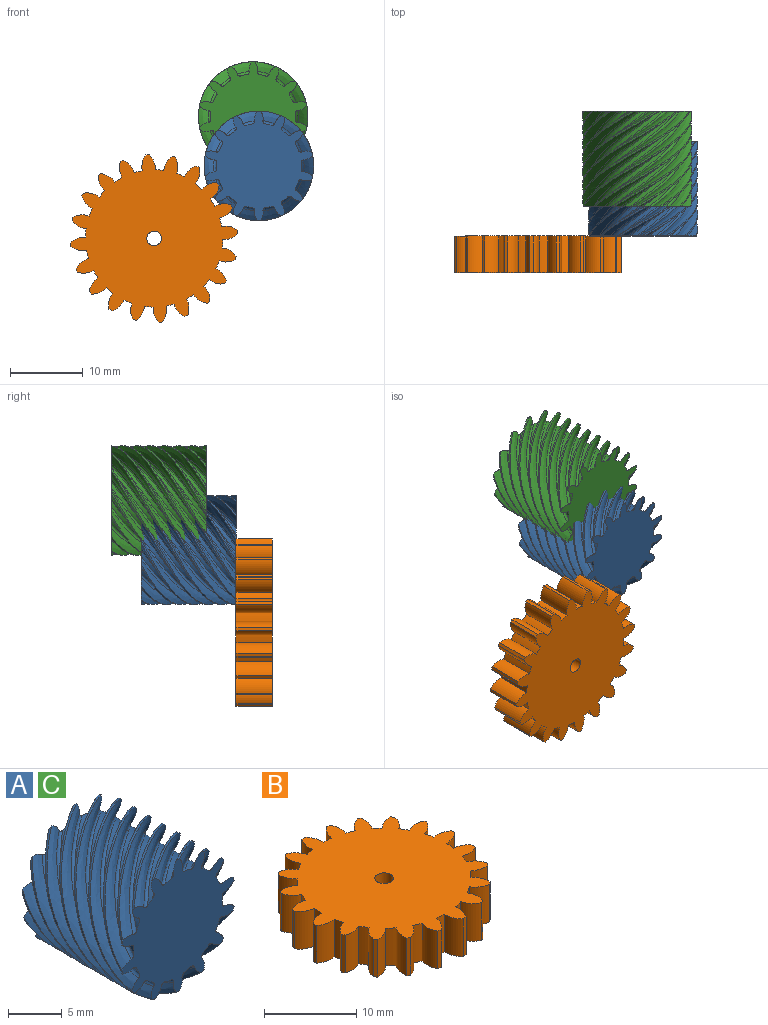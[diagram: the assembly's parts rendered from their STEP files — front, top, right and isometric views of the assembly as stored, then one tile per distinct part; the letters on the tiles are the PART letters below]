
ASSEMBLY  parts=3 mates=1
PART A: 114 faces, bbox 15.8x13.5x15.8 mm
  f0: cylinder r=5.81mm len=13mm, axis (0,1,0), area 11.1mm2, adj f14,f15,f19,f113
  f1: cylinder r=5.81mm len=13mm, axis (0,1,0), area 11.1mm2, adj f14,f15,f106,f110
  f2: cylinder r=5.81mm len=13mm, axis (0,1,0), area 11.1mm2, adj f14,f15,f99,f103
  f3: cylinder r=5.81mm len=13mm, axis (0,1,0), area 11.1mm2, adj f14,f15,f92,f96
  f4: cylinder r=5.81mm len=13mm, axis (0,1,0), area 11.1mm2, adj f14,f15,f85,f89
  f5: cylinder r=5.81mm len=13mm, axis (0,1,0), area 11.1mm2, adj f14,f15,f78,f82
  f6: cylinder r=5.81mm len=13mm, axis (0,1,0), area 11.1mm2, adj f14,f15,f71,f75
  f7: cylinder r=5.81mm len=13mm, axis (0,1,0), area 11.1mm2, adj f14,f15,f64,f68
  f8: cylinder r=5.81mm len=13mm, axis (0,1,0), area 11.1mm2, adj f14,f15,f57,f61
  f9: cylinder r=5.81mm len=13mm, axis (0,1,0), area 11.1mm2, adj f14,f15,f50,f54
  f10: cylinder r=5.81mm len=13mm, axis (0,1,0), area 11.1mm2, adj f14,f15,f43,f47
  f11: cylinder r=5.81mm len=13mm, axis (0,1,0), area 11.1mm2, adj f14,f15,f36,f40
  f12: cylinder r=5.81mm len=13mm, axis (0,1,0), area 11.1mm2, adj f14,f15,f29,f33
  f13: cylinder r=5.81mm len=13mm, axis (0,1,0), area 11.1mm2, adj f14,f15,f22,f26
  f14: plane 15.02x14.73mm, normal (0,-1,0), area 130.6mm2, adj f0,f1,f2,f3,f4,f5,f6,f7
  f15: plane 15.01x14.92mm, normal (0,1,0), area 129.4mm2, adj f0,f1,f2,f3,f4,f5,f6,f7
  f16: cylinder r=7.5mm len=14.99mm, axis (0,1,0), area 5.5mm2, adj f14,f15,f17,f18
  f17: bspline ~15.06x13.32mm, area 33mm2, adj f14,f15,f16,f22
  f18: bspline ~15.08x13.32mm, area 33mm2, adj f14,f15,f16,f19
  f19: bspline ~13.46x12.53mm, area 10.7mm2, adj f0,f14,f15,f18,f20
  f20: plane 0.44x0.4mm, normal (0,1,0), area 0mm2, adj f15,f19
  f21: plane 0.45x0.42mm, normal (0,1,0), area 0mm2, adj f15,f22
  f22: bspline ~13x12.36mm, area 10.7mm2, adj f13,f14,f17,f21
  f23: cylinder r=7.5mm len=14.35mm, axis (0,1,0), area 5.5mm2, adj f14,f15,f24,f25
  f24: bspline ~14.45x13.32mm, area 33mm2, adj f14,f15,f23,f29
  f25: bspline ~14.35x13.01mm, area 33mm2, adj f14,f15,f23,f26
  f26: bspline ~13.32x12.31mm, area 10.7mm2, adj f13,f14,f15,f25,f27
  f27: plane 0.45x0.34mm, normal (0,1,0), area 0mm2, adj f15,f26
  f28: plane 0.53x0.39mm, normal (0,1,0), area 0mm2, adj f15,f29
  f29: bspline ~13x11.51mm, area 10.7mm2, adj f12,f14,f24,f28
  f30: cylinder r=7.5mm len=13.13mm, axis (0,1,0), area 5.5mm2, adj f14,f15,f31,f32
  f31: bspline ~13.53x13.32mm, area 33mm2, adj f14,f15,f30,f36
  f32: bspline ~13.01x12.85mm, area 33mm2, adj f14,f15,f30,f33
  f33: bspline ~13.01x10.48mm, area 10.7mm2, adj f12,f14,f15,f32,f34
  f34: plane 0.5x0.31mm, normal (0,1,0), area 0mm2, adj f15,f33
  f35: plane 0.54x0.37mm, normal (0,1,0), area 0mm2, adj f15,f36
  f36: bspline ~13x11.09mm, area 10.7mm2, adj f11,f14,f31,f35
  f37: cylinder r=7.5mm len=14.72mm, axis (0,1,0), area 5.5mm2, adj f14,f15,f38,f39
  f38: bspline ~15.19x13.32mm, area 33mm2, adj f14,f15,f37,f43
  f39: bspline ~15.16x13.32mm, area 33mm2, adj f14,f15,f37,f40
  f40: bspline ~13.46x12.42mm, area 10.7mm2, adj f11,f14,f15,f39,f41
  f41: plane 0.46x0.41mm, normal (0,1,0), area 0mm2, adj f15,f40
  f42: plane 0.44x0.41mm, normal (0,1,0), area 0mm2, adj f15,f43
  f43: bspline ~13x12.26mm, area 10.8mm2, adj f10,f14,f38,f42
  f44: cylinder r=7.5mm len=14.86mm, axis (0,1,0), area 5.5mm2, adj f14,f15,f45,f46
  f45: bspline ~15.13x13.32mm, area 33mm2, adj f14,f15,f44,f50
  f46: bspline ~14.85x13.01mm, area 33mm2, adj f14,f15,f44,f47
  f47: bspline ~13.01x12.33mm, area 10.7mm2, adj f10,f14,f15,f46,f48
  f48: plane 0.45x0.34mm, normal (0,1,0), area 0mm2, adj f15,f47
  f49: plane 0.49x0.43mm, normal (0,1,0), area 0mm2, adj f15,f50
  f50: bspline ~13x12.08mm, area 10.7mm2, adj f9,f14,f45,f49
  f51: cylinder r=7.5mm len=13.49mm, axis (0,1,0), area 5.5mm2, adj f14,f15,f52,f53
  f52: bspline ~13.39x13.32mm, area 33mm2, adj f14,f15,f51,f57
  f53: bspline ~13.49x13.01mm, area 33mm2, adj f14,f15,f51,f54
  f54: bspline ~13.01x11.37mm, area 10.7mm2, adj f9,f14,f15,f53,f55
  f55: plane 0.49x0.33mm, normal (0,1,0), area 0mm2, adj f15,f54
  f56: plane 0.55x0.34mm, normal (0,1,0), area 0mm2, adj f15,f57
  f57: bspline ~13x10.67mm, area 10.7mm2, adj f8,f14,f52,f56
  f58: cylinder r=7.5mm len=14.09mm, axis (0,1,0), area 5.5mm2, adj f14,f15,f59,f60
  f59: bspline ~14.69x13.32mm, area 33mm2, adj f14,f15,f58,f64
  f60: bspline ~14.47x13.32mm, area 33mm2, adj f14,f15,f58,f61
  f61: bspline ~13.46x11.68mm, area 10.7mm2, adj f8,f14,f15,f60,f62
  f62: plane 0.49x0.36mm, normal (0,1,0), area 0mm2, adj f15,f61
  f63: plane 0.5x0.4mm, normal (0,1,0), area 0mm2, adj f15,f64
  f64: bspline ~13x11.82mm, area 10.7mm2, adj f7,f14,f59,f63
  f65: cylinder r=7.5mm len=14.99mm, axis (0,1,0), area 5.5mm2, adj f14,f15,f66,f67
  f66: bspline ~15.06x13.32mm, area 33mm2, adj f14,f15,f65,f71
  f67: bspline ~15.08x13.32mm, area 33mm2, adj f14,f15,f65,f68
  f68: bspline ~13.46x12.53mm, area 10.7mm2, adj f7,f14,f15,f67,f69
  f69: plane 0.44x0.4mm, normal (0,1,0), area 0mm2, adj f15,f68
  f70: plane 0.44x0.42mm, normal (0,1,0), area 0mm2, adj f15,f71
  f71: bspline ~13x12.36mm, area 10.7mm2, adj f6,f14,f66,f70
  f72: cylinder r=7.5mm len=14.35mm, axis (0,1,0), area 5.5mm2, adj f14,f15,f73,f74
  f73: bspline ~14.45x13.32mm, area 33mm2, adj f14,f15,f72,f78
  f74: bspline ~14.35x13.01mm, area 33mm2, adj f14,f15,f72,f75
  f75: bspline ~13.32x12.31mm, area 10.7mm2, adj f6,f14,f15,f74,f76
  f76: plane 0.45x0.34mm, normal (0,1,0), area 0mm2, adj f15,f75
  f77: plane 0.53x0.39mm, normal (0,1,0), area 0mm2, adj f15,f78
  f78: bspline ~13x11.51mm, area 10.7mm2, adj f5,f14,f73,f77
  f79: cylinder r=7.5mm len=13.13mm, axis (0,1,0), area 5.5mm2, adj f14,f15,f80,f81
  f80: bspline ~13.53x13.32mm, area 33mm2, adj f14,f15,f79,f85
  f81: bspline ~13.01x12.85mm, area 33mm2, adj f14,f15,f79,f82
  f82: bspline ~13.01x10.48mm, area 10.7mm2, adj f5,f14,f15,f81,f83
  f83: plane 0.5x0.31mm, normal (0,1,0), area 0mm2, adj f15,f82
  f84: plane 0.54x0.37mm, normal (0,1,0), area 0mm2, adj f15,f85
  f85: bspline ~13x11.09mm, area 10.7mm2, adj f4,f14,f80,f84
  f86: cylinder r=7.5mm len=14.72mm, axis (0,1,0), area 5.5mm2, adj f14,f15,f87,f88
  f87: bspline ~15.19x13.32mm, area 33mm2, adj f14,f15,f86,f92
  f88: bspline ~15.16x13.32mm, area 33mm2, adj f14,f15,f86,f89
  f89: bspline ~13.46x12.42mm, area 10.7mm2, adj f4,f14,f15,f88,f90
  f90: plane 0.46x0.41mm, normal (0,1,0), area 0mm2, adj f15,f89
  f91: plane 0.44x0.41mm, normal (0,1,0), area 0mm2, adj f15,f92
  f92: bspline ~13x12.26mm, area 10.8mm2, adj f3,f14,f87,f91
  f93: cylinder r=7.5mm len=14.86mm, axis (0,1,0), area 5.5mm2, adj f14,f15,f94,f95
  f94: bspline ~15.13x13.32mm, area 33mm2, adj f14,f15,f93,f99
  f95: bspline ~14.85x13.01mm, area 33mm2, adj f14,f15,f93,f96
  f96: bspline ~13.01x12.33mm, area 10.7mm2, adj f3,f14,f15,f95,f97
  f97: plane 0.45x0.34mm, normal (0,1,0), area 0mm2, adj f15,f96
  f98: plane 0.49x0.43mm, normal (0,1,0), area 0mm2, adj f15,f99
  f99: bspline ~13x12.08mm, area 10.7mm2, adj f2,f14,f94,f98
  f100: cylinder r=7.5mm len=13.49mm, axis (0,1,0), area 5.5mm2, adj f14,f15,f101,f102
  f101: bspline ~13.39x13.32mm, area 33mm2, adj f14,f15,f100,f106
  f102: bspline ~13.49x13.01mm, area 33mm2, adj f14,f15,f100,f103
  f103: bspline ~13.01x11.37mm, area 10.7mm2, adj f2,f14,f15,f102,f104
  f104: plane 0.49x0.33mm, normal (0,1,0), area 0mm2, adj f15,f103
  f105: plane 0.55x0.34mm, normal (0,1,0), area 0mm2, adj f15,f106
  f106: bspline ~13x10.67mm, area 10.7mm2, adj f1,f14,f101,f105
  f107: cylinder r=7.5mm len=14.09mm, axis (0,1,0), area 5.5mm2, adj f14,f15,f108,f109
  f108: bspline ~14.69x13.32mm, area 33mm2, adj f14,f15,f107,f113
  f109: bspline ~14.47x13.32mm, area 33mm2, adj f14,f15,f107,f110
  f110: bspline ~13.46x11.68mm, area 10.7mm2, adj f1,f14,f15,f109,f111
  f111: plane 0.49x0.36mm, normal (0,1,0), area 0mm2, adj f15,f110
  f112: plane 0.5x0.4mm, normal (0,1,0), area 0mm2, adj f15,f113
  f113: bspline ~13x11.82mm, area 10.7mm2, adj f0,f14,f108,f112
PART B: 83 faces, bbox 23x23x5 mm
  f0: cylinder r=2.61mm len=5mm, axis (0,0,-1), area 11.5mm2, adj f1,f79,f81,f82
  f1: cylinder r=9.41mm len=5mm, axis (0,0,-1), area 5.9mm2, adj f0,f2,f81,f82
  f2: cylinder r=2.61mm len=5mm, axis (0,0,-1), area 11.5mm2, adj f1,f3,f81,f82
  f3: plane 5x0.41mm, normal (-0.38,0.92,0), area 2.2mm2, adj f2,f4,f81,f82
  f4: cylinder r=2.61mm len=5mm, axis (0,0,-1), area 11.5mm2, adj f3,f5,f81,f82
  f5: cylinder r=9.41mm len=5mm, axis (0,0,-1), area 5.9mm2, adj f4,f6,f81,f82
  f6: cylinder r=2.61mm len=5mm, axis (0,0,-1), area 11.5mm2, adj f5,f7,f81,f82
  f7: plane 5x0.34mm, normal (-0.65,0.76,0), area 2.2mm2, adj f6,f8,f81,f82
  f8: cylinder r=2.61mm len=5mm, axis (0,0,-1), area 11.5mm2, adj f7,f9,f81,f82
  f9: cylinder r=9.41mm len=5mm, axis (0,0,-1), area 5.9mm2, adj f8,f10,f81,f82
  f10: cylinder r=2.61mm len=5mm, axis (0,0,-1), area 11.5mm2, adj f9,f11,f81,f82
  f11: plane 5x0.38mm, normal (-0.85,0.52,0), area 2.2mm2, adj f10,f12,f81,f82
  f12: cylinder r=2.61mm len=5mm, axis (0,0,-1), area 11.5mm2, adj f11,f13,f81,f82
  f13: cylinder r=9.41mm len=5mm, axis (0,0,-1), area 5.9mm2, adj f12,f14,f81,f82
  f14: cylinder r=2.61mm len=5mm, axis (0,0,-1), area 11.5mm2, adj f13,f15,f81,f82
  f15: plane 5x0.43mm, normal (-0.97,0.23,0), area 2.2mm2, adj f14,f16,f81,f82
  f16: cylinder r=2.61mm len=5mm, axis (0,0,-1), area 11.5mm2, adj f15,f17,f81,f82
  f17: cylinder r=9.41mm len=5mm, axis (0,0,-1), area 5.9mm2, adj f16,f18,f81,f82
  f18: cylinder r=2.61mm len=5mm, axis (0,0,-1), area 11.5mm2, adj f17,f19,f81,f82
  f19: plane 5x0.44mm, normal (-1,-0.08,0), area 2.2mm2, adj f18,f20,f81,f82
  f20: cylinder r=2.61mm len=5mm, axis (0,0,-1), area 11.5mm2, adj f19,f21,f81,f82
  f21: cylinder r=9.41mm len=5mm, axis (0,0,-1), area 5.9mm2, adj f20,f22,f81,f82
  f22: cylinder r=2.61mm len=5mm, axis (0,0,-1), area 11.5mm2, adj f21,f23,f81,f82
  f23: plane 5x0.41mm, normal (-0.92,-0.38,0), area 2.2mm2, adj f22,f24,f81,f82
  f24: cylinder r=2.61mm len=5mm, axis (0,0,-1), area 11.5mm2, adj f23,f25,f81,f82
  f25: cylinder r=9.41mm len=5mm, axis (0,0,-1), area 5.9mm2, adj f24,f26,f81,f82
  f26: cylinder r=2.61mm len=5mm, axis (0,0,-1), area 11.5mm2, adj f25,f27,f81,f82
  f27: plane 5x0.34mm, normal (-0.76,-0.65,0), area 2.2mm2, adj f26,f28,f81,f82
  f28: cylinder r=2.61mm len=5mm, axis (0,0,-1), area 11.5mm2, adj f27,f29,f81,f82
  f29: cylinder r=9.41mm len=5mm, axis (0,0,-1), area 5.9mm2, adj f28,f30,f81,f82
  f30: cylinder r=2.61mm len=5mm, axis (0,0,-1), area 11.5mm2, adj f29,f31,f81,f82
  f31: plane 5x0.38mm, normal (-0.52,-0.85,0), area 2.2mm2, adj f30,f32,f81,f82
  f32: cylinder r=2.61mm len=5mm, axis (0,0,-1), area 11.5mm2, adj f31,f33,f81,f82
  f33: cylinder r=9.41mm len=5mm, axis (0,0,-1), area 5.9mm2, adj f32,f34,f81,f82
  f34: cylinder r=2.61mm len=5mm, axis (0,0,-1), area 11.5mm2, adj f33,f35,f81,f82
  f35: plane 5x0.43mm, normal (-0.23,-0.97,0), area 2.2mm2, adj f34,f36,f81,f82
  f36: cylinder r=2.61mm len=5mm, axis (0,0,-1), area 11.5mm2, adj f35,f37,f81,f82
  f37: cylinder r=9.41mm len=5mm, axis (0,0,-1), area 5.9mm2, adj f36,f38,f81,f82
  f38: cylinder r=2.61mm len=5mm, axis (0,0,-1), area 11.5mm2, adj f37,f39,f81,f82
  f39: plane 5x0.44mm, normal (0.08,-1,0), area 2.2mm2, adj f38,f40,f81,f82
  f40: cylinder r=2.61mm len=5mm, axis (0,0,-1), area 11.5mm2, adj f39,f41,f81,f82
  f41: cylinder r=9.41mm len=5mm, axis (0,0,-1), area 5.9mm2, adj f40,f42,f81,f82
  f42: cylinder r=2.61mm len=5mm, axis (0,0,-1), area 11.5mm2, adj f41,f43,f81,f82
  f43: plane 5x0.41mm, normal (0.38,-0.92,0), area 2.2mm2, adj f42,f44,f81,f82
  f44: cylinder r=2.61mm len=5mm, axis (0,0,-1), area 11.5mm2, adj f43,f45,f81,f82
  f45: cylinder r=9.41mm len=5mm, axis (0,0,-1), area 5.9mm2, adj f44,f46,f81,f82
  f46: cylinder r=2.61mm len=5mm, axis (0,0,-1), area 11.5mm2, adj f45,f47,f81,f82
  f47: plane 5x0.34mm, normal (0.65,-0.76,0), area 2.2mm2, adj f46,f48,f81,f82
  f48: cylinder r=2.61mm len=5mm, axis (0,0,-1), area 11.5mm2, adj f47,f49,f81,f82
  f49: cylinder r=9.41mm len=5mm, axis (0,0,-1), area 5.9mm2, adj f48,f50,f81,f82
  f50: cylinder r=2.61mm len=5mm, axis (0,0,-1), area 11.5mm2, adj f49,f51,f81,f82
  f51: plane 5x0.38mm, normal (0.85,-0.52,0), area 2.2mm2, adj f50,f52,f81,f82
  f52: cylinder r=2.61mm len=5mm, axis (0,0,-1), area 11.5mm2, adj f51,f53,f81,f82
  f53: cylinder r=9.41mm len=5mm, axis (0,0,-1), area 5.9mm2, adj f52,f54,f81,f82
  f54: cylinder r=2.61mm len=5mm, axis (0,0,-1), area 11.5mm2, adj f53,f55,f81,f82
  f55: plane 5x0.43mm, normal (0.97,-0.23,0), area 2.2mm2, adj f54,f56,f81,f82
  f56: cylinder r=2.61mm len=5mm, axis (0,0,-1), area 11.5mm2, adj f55,f57,f81,f82
  f57: cylinder r=9.41mm len=5mm, axis (0,0,-1), area 5.9mm2, adj f56,f58,f81,f82
  f58: cylinder r=2.61mm len=5mm, axis (0,0,-1), area 11.5mm2, adj f57,f59,f81,f82
  f59: plane 5x0.44mm, normal (1,0.08,0), area 2.2mm2, adj f58,f60,f81,f82
  f60: cylinder r=2.61mm len=5mm, axis (0,0,-1), area 11.5mm2, adj f59,f61,f81,f82
  f61: cylinder r=9.41mm len=5mm, axis (0,0,-1), area 5.9mm2, adj f60,f62,f81,f82
  f62: cylinder r=2.61mm len=5mm, axis (0,0,-1), area 11.5mm2, adj f61,f63,f81,f82
  f63: plane 5x0.41mm, normal (0.92,0.38,0), area 2.2mm2, adj f62,f64,f81,f82
  f64: cylinder r=2.61mm len=5mm, axis (0,0,-1), area 11.5mm2, adj f63,f65,f81,f82
  f65: cylinder r=9.41mm len=5mm, axis (0,0,-1), area 5.9mm2, adj f64,f66,f81,f82
  f66: cylinder r=2.61mm len=5mm, axis (0,0,-1), area 11.5mm2, adj f65,f67,f81,f82
  f67: plane 5x0.34mm, normal (0.76,0.65,0), area 2.2mm2, adj f66,f68,f81,f82
  f68: cylinder r=2.61mm len=5mm, axis (0,0,-1), area 11.5mm2, adj f67,f69,f81,f82
  f69: cylinder r=9.41mm len=5mm, axis (0,0,-1), area 5.9mm2, adj f68,f70,f81,f82
  f70: cylinder r=2.61mm len=5mm, axis (0,0,-1), area 11.5mm2, adj f69,f71,f81,f82
  f71: plane 5x0.38mm, normal (0.52,0.85,0), area 2.2mm2, adj f70,f72,f81,f82
  f72: cylinder r=2.61mm len=5mm, axis (0,0,-1), area 11.5mm2, adj f71,f73,f81,f82
  f73: cylinder r=9.41mm len=5mm, axis (0,0,-1), area 5.9mm2, adj f72,f74,f81,f82
  f74: cylinder r=2.61mm len=5mm, axis (0,0,-1), area 11.5mm2, adj f73,f75,f81,f82
  f75: plane 5x0.43mm, normal (0.23,0.97,0), area 2.2mm2, adj f74,f76,f81,f82
  f76: cylinder r=2.61mm len=5mm, axis (0,0,-1), area 11.5mm2, adj f75,f77,f81,f82
  f77: cylinder r=9.41mm len=5mm, axis (0,0,-1), area 5.9mm2, adj f76,f78,f81,f82
  f78: cylinder r=2.61mm len=5mm, axis (0,0,-1), area 11.5mm2, adj f77,f79,f81,f82
  f79: plane 5x0.44mm, normal (-0.08,1,0), area 2.2mm2, adj f0,f78,f81,f82
  f80: cylinder r=1mm len=5mm, axis (0,0,-1), area 31.4mm2, adj f81,f82
  f81: plane 22.96x22.96mm, normal (0,0,1), area 336.5mm2, adj f0,f1,f2,f3,f4,f5,f6,f7
  f82: plane 22.96x22.96mm, normal (0,0,-1), area 336.5mm2, adj f0,f1,f2,f3,f4,f5,f6,f7
PART C: same geometry as A
PLACE A at identity
PLACE B rot(axis=(1,0,0),90deg) t=(-14.35,-6.49,-9.94)mm
PLACE C t=(-0.78,4.06,6.76)mm
MATE parallel B.f81 <-> A.f14  axis (0,-1,0) through (-14.19,-11.49,-0.53)mm
